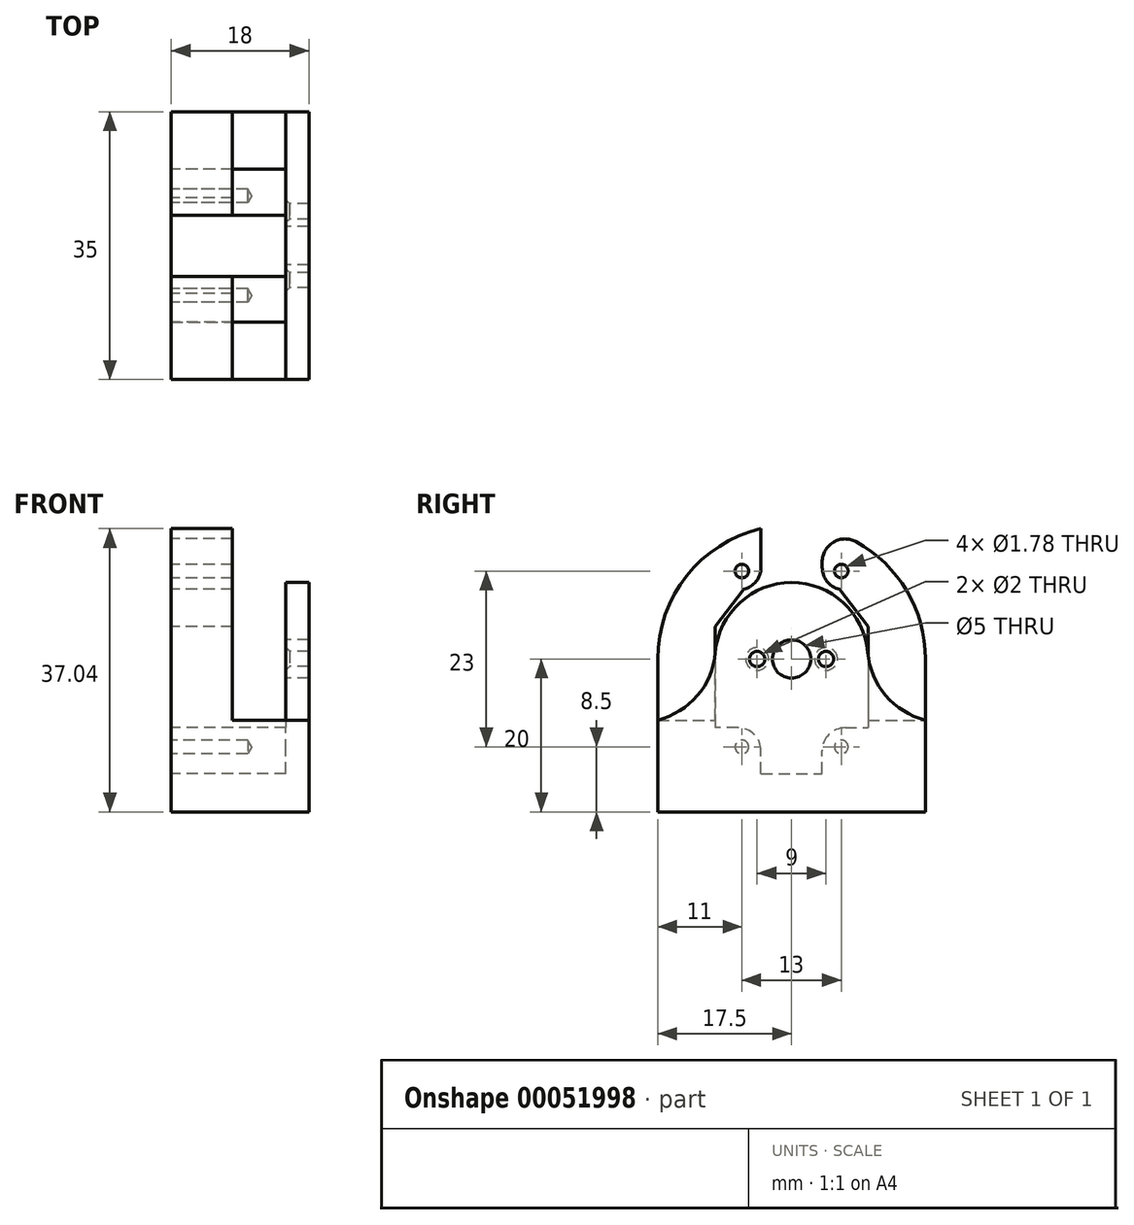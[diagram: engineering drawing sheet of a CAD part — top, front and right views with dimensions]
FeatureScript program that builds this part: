
annotation { "Feature Type Name" : "Feature", "Feature Type Description" : "" }
export const myFeature = defineFeature(function(context is Context, id is Id, definition is map)
    precondition{}
    {
        {
            var Q0;
            Q0=qCreatedBy(makeId("Right.planeOp"),FACE);
            var sketch = newSketch(context, id + "F0", { "sketchPlane" : qUnion([Q0])});
            skLineSegment(sketch, "E0.bottom", {"start": v(-17.5, 0) * mm, "end": v(17.5, 0) * mm});
            skLineSegment(sketch, "E0.left", {"start": v(-17.5, 0) * mm, "end": v(-17.5, 20) * mm});
            skLineSegment(sketch, "E0.right", {"start": v(17.5, 0) * mm, "end": v(17.5, 20) * mm});
            skArc(sketch, "E1", {"start": v(17.5, 20) * mm, "mid": v(0, 37.5) * mm, "end": v(-17.5, 20) * mm});
            skCircle(sketch, "E2", {"center": v(0, 20) * mm, "radius": 2.5 * mm});
            skSolve(sketch);
        }
        {
            var Q0;
            Q0=makeQuery(id+"F0.imprint","IMPRINT",FACE,{"disambiguationData":[TD([[makeQuery(id+"F0.imprint","IMPRINT",EDGE,{"derivedFrom":sQuery(id+"F0.wireOp",EDGE,"E0.bottom")}),1.0]])]});
            extrude(context, id + "F1", {"entities" : qUnion([Q0]), "endBound" : BoundingType.SYMMETRIC, "depth" : 18 * mm});
        }
        {
            var Q0;
            Q0=makeQuery(id+"F1.opExtrude","CAP_FACE",FACE,{"disambiguationData":[OSD([sQuery(id+"F0.wireOp",EDGE,"E0.bottom"),sQuery(id+"F0.wireOp",EDGE,"E0.left"),sQuery(id+"F0.wireOp",EDGE,"E0.right"),sQuery(id+"F0.wireOp",EDGE,"E1")])],"isStart":true});
            var sketch = newSketch(context, id + "F2", { "sketchPlane" : qUnion([Q0])});
            skPoint(sketch, "E3", {"position": v(-6.5, 31.5) * mm});
            skPoint(sketch, "E4", {"position": v(6.5, 31.5) * mm});
            skPoint(sketch, "E5", {"position": v(6.5, 8.5) * mm});
            skPoint(sketch, "E6", {"position": v(-6.5, 8.5) * mm});
            skLineSegment(sketch, "E7", {"start": v(0, 20) * mm, "end": v(0, 45.84) * mm, "construction": true});
            skLineSegment(sketch, "E8", {"start": v(0, 20) * mm, "end": v(5.58, 20) * mm, "construction": true});
            skSolve(sketch);
        }
        {
            var Q0;
            Q0=sQuery(id+"F2.wireOp",VERTEX,"E6");
            var Q1;
            Q1=sQuery(id+"F2.wireOp",VERTEX,"E5");
            var Q2;
            Q2=sQuery(id+"F2.wireOp",VERTEX,"E4");
            var Q3;
            Q3=sQuery(id+"F2.wireOp",VERTEX,"E3");
            var Q4;
            Q4=makeQuery(id+"F1.opExtrude","SWEPT_BODY",BODY,{"disambiguationData":[OSD([sQuery(id+"F0.wireOp",EDGE,"E0.bottom"),sQuery(id+"F0.wireOp",EDGE,"E0.left"),sQuery(id+"F0.wireOp",EDGE,"E0.right"),sQuery(id+"F0.wireOp",EDGE,"E1")])]});
            hole(context, id + "F3", {"style" : HoleStyle.SIMPLE, "holeDiameter" : 1.78 * mm, "endStyle" : HoleEndStyle.BLIND, "holeDepth" : 10 * mm, "locations" : qUnion([Q0, Q1, Q2, Q3]), "scope" : qUnion([Q4])});
        }
        {
            var Q0;
            Q0=makeQuery(id+"F1.opExtrude","CAP_FACE",FACE,{"disambiguationData":[OSD([sQuery(id+"F0.wireOp",EDGE,"E0.bottom"),sQuery(id+"F0.wireOp",EDGE,"E0.left"),sQuery(id+"F0.wireOp",EDGE,"E0.right"),sQuery(id+"F0.wireOp",EDGE,"E1"),sQuery(id+"F0.wireOp",EDGE,"E2")])],"isStart":true});
            var sketch = newSketch(context, id + "F4", { "sketchPlane" : qUnion([Q0])});
            skLineSegment(sketch, "E9.rect.bottom", {"start": v(4, 35) * mm, "end": v(-4, 35) * mm});
            skLineSegment(sketch, "E9.rect.top", {"start": v(4, 5) * mm, "end": v(-4, 5) * mm});
            skLineSegment(sketch, "E9.rect.left", {"start": v(10, 29) * mm, "end": v(10, 11) * mm});
            skLineSegment(sketch, "E9.rect.right", {"start": v(-10, 29) * mm, "end": v(-10, 11) * mm});
            skPoint(sketch, "E9.rect.middle", {"position": v(0, 20) * mm});
            skLineSegment(sketch, "E10", {"start": v(4, 35) * mm, "end": v(4, 32) * mm});
            skLineSegment(sketch, "E11", {"start": v(7, 29) * mm, "end": v(10, 29) * mm});
            skArc(sketch, "E12", {"start": v(4, 32) * mm, "mid": v(4.88, 29.88) * mm, "end": v(7, 29) * mm});
            skLineSegment(sketch, "E13", {"start": v(0, 51.45) * mm, "end": v(0, 20) * mm, "construction": true});
            skLineSegment(sketch, "E14", {"start": v(0, 20) * mm, "end": v(35.14, 20) * mm, "construction": true});
            skPoint(sketch, "E15.orphan", {"position": v(10, 35) * mm});
            skArc(sketch, "E16.MirrorCS", {"start": v(-4, 32) * mm, "mid": v(-4.88, 29.88) * mm, "end": v(-7, 29) * mm});
            skLineSegment(sketch, "E17.MirrorCS", {"start": v(-7, 29) * mm, "end": v(-10, 29) * mm});
            skLineSegment(sketch, "E18.MirrorCS", {"start": v(-4, 35) * mm, "end": v(-4, 32) * mm});
            skLineSegment(sketch, "E19.MirrorCS", {"start": v(7, 11) * mm, "end": v(10, 11) * mm});
            skLineSegment(sketch, "E20.MirrorCS", {"start": v(4, 5) * mm, "end": v(4, 8) * mm});
            skArc(sketch, "E21.MirrorCS", {"start": v(4, 8) * mm, "mid": v(4.88, 10.12) * mm, "end": v(7, 11) * mm});
            skLineSegment(sketch, "E22.MirrorCS", {"start": v(-4, 5) * mm, "end": v(-4, 8) * mm});
            skLineSegment(sketch, "E23.MirrorCS", {"start": v(-7, 11) * mm, "end": v(-10, 11) * mm});
            skArc(sketch, "E24.MirrorCS", {"start": v(-4, 8) * mm, "mid": v(-4.88, 10.12) * mm, "end": v(-7, 11) * mm});
            skPoint(sketch, "E25.orphan", {"position": v(-10, 35) * mm});
            skPoint(sketch, "E26.orphan", {"position": v(-10, 5) * mm});
            skPoint(sketch, "E27.orphan", {"position": v(10, 5) * mm});
            skSolve(sketch);
        }
        {
            var Q0;
            Q0 = qSketchRegion(id + "F4", true);
            extrude(context, id + "F5", {"entities" : qUnion([Q0]), "operationType" : NewBodyOperationType.REMOVE, "oppositeDirection" : true, "depth" : 15 * mm});
        }
        {
            var Q0;
            Q0=makeQuery(id+"F1.opExtrude","CAP_FACE",FACE,{"disambiguationData":[OSD([sQuery(id+"F0.wireOp",EDGE,"E0.bottom"),sQuery(id+"F0.wireOp",EDGE,"E0.left"),sQuery(id+"F0.wireOp",EDGE,"E0.right"),sQuery(id+"F0.wireOp",EDGE,"E1"),sQuery(id+"F0.wireOp",EDGE,"E2")])],"isStart":false});
            var sketch = newSketch(context, id + "F6", { "sketchPlane" : qUnion([Q0])});
            skArc(sketch, "E28", {"start": v(10, 20) * mm, "mid": v(0, 30) * mm, "end": v(-10, 20) * mm});
            skArc(sketch, "E29", {"start": v(17.5, 20) * mm, "mid": v(0, 37.5) * mm, "end": v(-17.5, 20) * mm});
            skLineSegment(sketch, "E30", {"start": v(-17.5, 20) * mm, "end": v(-17.5, 12) * mm});
            skLineSegment(sketch, "E31", {"start": v(-17.5, 12) * mm, "end": v(-10, 12) * mm});
            skLineSegment(sketch, "E32", {"start": v(-10, 12) * mm, "end": v(-10, 20) * mm});
            skLineSegment(sketch, "E33", {"start": v(10, 20) * mm, "end": v(10, 12) * mm});
            skLineSegment(sketch, "E34", {"start": v(10, 12) * mm, "end": v(17.5, 12) * mm});
            skLineSegment(sketch, "E35", {"start": v(17.5, 12) * mm, "end": v(17.5, 20) * mm});
            skSolve(sketch);
        }
        {
            var Q0;
            Q0=makeQuery(id+"F6.imprint","IMPRINT",FACE,{"disambiguationData":[TD([[makeQuery(id+"F6.imprint","IMPRINT",EDGE,{"derivedFrom":sQuery(id+"F6.wireOp",EDGE,"d0672cb3-e5da-4a65-a351-25e1d119db8f")}),1.0]])]});
            var Q1;
            Q1=makeQuery(id+"F6.imprint","IMPRINT",FACE,{"disambiguationData":[TD([[makeQuery(id+"F6.imprint","IMPRINT",EDGE,{"derivedFrom":sQuery(id+"F6.wireOp",EDGE,"E28")}),-1.0]])]});
            extrude(context, id + "F7", {"entities" : qUnion([Q0, Q1]), "operationType" : NewBodyOperationType.REMOVE, "oppositeDirection" : true, "depth" : 10 * mm});
        }
        {
            var Q0;
            Q0=makeQuery(id+"F5.boolean.opBoolean","COPY",FACE,{"derivedFrom":makeQuery(id+"F5.opExtrude","CAP_FACE",FACE,{"disambiguationData":[OSD([sQuery(id+"F4.wireOp",EDGE,"E9.rect.bottom"),sQuery(id+"F4.wireOp",EDGE,"E9.rect.top"),sQuery(id+"F4.wireOp",EDGE,"E9.rect.left"),sQuery(id+"F4.wireOp",EDGE,"E9.rect.right"),sQuery(id+"F4.wireOp",EDGE,"E16.MirrorCS"),sQuery(id+"F4.wireOp",EDGE,"E17.MirrorCS"),sQuery(id+"F4.wireOp",EDGE,"E18.MirrorCS"),sQuery(id+"F4.wireOp",EDGE,"E10"),sQuery(id+"F4.wireOp",EDGE,"E12"),sQuery(id+"F4.wireOp",EDGE,"E11"),sQuery(id+"F4.wireOp",EDGE,"E19.MirrorCS"),sQuery(id+"F4.wireOp",EDGE,"E20.MirrorCS"),sQuery(id+"F4.wireOp",EDGE,"E21.MirrorCS"),sQuery(id+"F4.wireOp",EDGE,"E22.MirrorCS"),sQuery(id+"F4.wireOp",EDGE,"E23.MirrorCS"),sQuery(id+"F4.wireOp",EDGE,"E24.MirrorCS")])],"isStart":false})});
            var sketch = newSketch(context, id + "F8", { "sketchPlane" : qUnion([Q0])});
            skLineSegment(sketch, "E36", {"start": v(0, 20) * mm, "end": v(0, 32.94) * mm, "construction": true});
            skPoint(sketch, "E37.MirrorP", {"position": v(4.5, 20) * mm});
            skPoint(sketch, "E38.MirrorP", {"position": v(-4.5, 20) * mm});
            skSolve(sketch);
        }
        {
            var Q0;
            Q0=sQuery(id+"F8.wireOp",VERTEX,"E37.MirrorP");
            var Q1;
            Q1=sQuery(id+"F8.wireOp",VERTEX,"E38.MirrorP");
            var Q2;
            Q2=makeQuery(id+"F1.opExtrude","SWEPT_BODY",BODY,{"disambiguationData":[OSD([sQuery(id+"F0.wireOp",EDGE,"E0.bottom"),sQuery(id+"F0.wireOp",EDGE,"E0.left"),sQuery(id+"F0.wireOp",EDGE,"E0.right"),sQuery(id+"F0.wireOp",EDGE,"E1"),sQuery(id+"F0.wireOp",EDGE,"E2")])]});
            hole(context, id + "F9", {"style" : HoleStyle.C_SINK, "holeDiameter" : 2 * mm, "cSinkDiameter" : 3 * mm, "endStyle" : HoleEndStyle.THROUGH, "locations" : qUnion([Q0, Q1]), "scope" : qUnion([Q2]), "cSinkAngle" : 90 * degree});
        }
        {
            var Q0;
            {var subQ0=sQuery(id+"F6.wireOp",EDGE,"E31");var subQ2=sQuery(id+"F6.wireOp",EDGE,"E32");Q0=makeQuery(id+"F7.boolean.opBoolean","COPY",EDGE,{"disambiguationData":[TD([makeQuery(id+"F1.opExtrude","CAP_FACE",FACE,{"disambiguationData":[OSD([sQuery(id+"F0.wireOp",EDGE,"E0.bottom"),sQuery(id+"F0.wireOp",EDGE,"E0.left"),sQuery(id+"F0.wireOp",EDGE,"E0.right"),sQuery(id+"F0.wireOp",EDGE,"E1"),sQuery(id+"F0.wireOp",EDGE,"E2")])],"isStart":false})])],"derivedFrom":makeQuery(id+"F7.opExtrude","SWEPT_EDGE",EDGE,{"disambiguationData":[OSD([subQ0,subQ2])]})});}
            var Q1;
            {var subQ0=sQuery(id+"F6.wireOp",EDGE,"E33");var subQ1=sQuery(id+"F6.wireOp",EDGE,"E34");Q1=makeQuery(id+"F7.boolean.opBoolean","COPY",EDGE,{"disambiguationData":[TD([makeQuery(id+"F1.opExtrude","CAP_FACE",FACE,{"disambiguationData":[OSD([sQuery(id+"F0.wireOp",EDGE,"E0.bottom"),sQuery(id+"F0.wireOp",EDGE,"E0.left"),sQuery(id+"F0.wireOp",EDGE,"E0.right"),sQuery(id+"F0.wireOp",EDGE,"E1"),sQuery(id+"F0.wireOp",EDGE,"E2")])],"isStart":false})])],"derivedFrom":makeQuery(id+"F7.opExtrude","SWEPT_EDGE",EDGE,{"disambiguationData":[OSD([subQ0,subQ1])]})});}
            fillet(context, id + "F10", {"entities" : qUnion([Q0, Q1]), "radius" : 10 * mm, "tangentPropagation" : true, "allowEdgeOverflow" : false});
        }
        {
            var Q0;
            Q0=makeQuery(id+"F1.opExtrude","CAP_FACE",FACE,{"disambiguationData":[OSD([sQuery(id+"F0.wireOp",EDGE,"E0.bottom"),sQuery(id+"F0.wireOp",EDGE,"E0.left"),sQuery(id+"F0.wireOp",EDGE,"E0.right"),sQuery(id+"F0.wireOp",EDGE,"E1"),sQuery(id+"F0.wireOp",EDGE,"E2")])],"isStart":true});
            var sketch = newSketch(context, id + "F11", { "sketchPlane" : qUnion([Q0])});
            skLineSegment(sketch, "E39.bottom", {"start": v(-4, 35) * mm, "end": v(4, 35) * mm});
            skLineSegment(sketch, "E39.top", {"start": v(-4, 43.78) * mm, "end": v(4, 43.78) * mm});
            skLineSegment(sketch, "E39.left", {"start": v(-4, 35) * mm, "end": v(-4, 43.78) * mm});
            skLineSegment(sketch, "E39.right", {"start": v(4, 35) * mm, "end": v(4, 43.78) * mm});
            skSolve(sketch);
        }
        {
            var Q0;
            {var subQ0=sQuery(id+"F11.wireOp",EDGE,"E39.bottom");Q0=makeQuery(id+"F11.imprint","IMPRINT",FACE,{"disambiguationData":[TD([[makeQuery(id+"F11.imprint","IMPRINT",EDGE,{"derivedFrom":subQ0}),-1.0]])]});}
            extrude(context, id + "F12", {"entities" : qUnion([Q0]), "operationType" : NewBodyOperationType.REMOVE, "oppositeDirection" : true, "depth" : 25 * mm});
        }
        {
            var Q0;
            Q0=makeQuery(id+"F12.boolean.opBoolean","COPY",EDGE,{"derivedFrom":makeQuery(id+"F12.opExtrude","SWEPT_EDGE",EDGE,{"disambiguationData":[OSD([sQuery(id+"F0.wireOp",EDGE,"E1"),sQuery(id+"F11.wireOp",EDGE,"E39.right")])]})});
            var Q1;
            Q1=makeQuery(id+"F12.boolean.opBoolean","COPY",EDGE,{"derivedFrom":makeQuery(id+"F12.opExtrude","SWEPT_EDGE",EDGE,{"disambiguationData":[OSD([sQuery(id+"F0.wireOp",EDGE,"E1"),sQuery(id+"F11.wireOp",EDGE,"E39.left")])]})});
            fillet(context, id + "F13", {"entities" : qUnion([Q0, Q1]), "radius" : 3 * mm, "tangentPropagation" : true, "allowEdgeOverflow" : false});
        }
        {
            var Q0;
            Q0=makeQuery(id+"F5.boolean.opBoolean","COPY",EDGE,{"derivedFrom":makeQuery(id+"F5.opExtrude","SWEPT_EDGE",EDGE,{"disambiguationData":[OSD([sQuery(id+"F4.wireOp",EDGE,"E9.rect.right"),sQuery(id+"F4.wireOp",EDGE,"E17.MirrorCS")])]})});
            var Q1;
            Q1=makeQuery(id+"F5.boolean.opBoolean","COPY",EDGE,{"derivedFrom":makeQuery(id+"F5.opExtrude","SWEPT_EDGE",EDGE,{"disambiguationData":[OSD([sQuery(id+"F4.wireOp",EDGE,"E9.rect.left"),sQuery(id+"F4.wireOp",EDGE,"E11")])]})});
            chamfer(context, id + "F14", {"entities" : qUnion([Q0, Q1]), "width" : 5 * mm, "tangentPropagation" : true});
        }
    });
